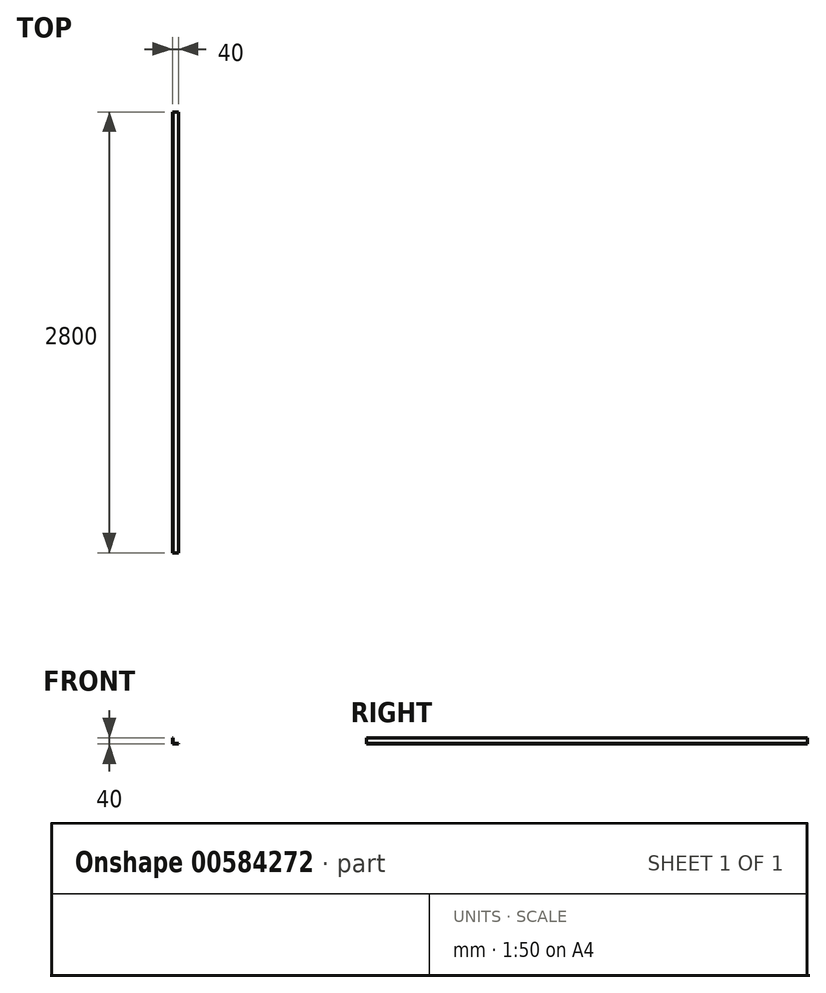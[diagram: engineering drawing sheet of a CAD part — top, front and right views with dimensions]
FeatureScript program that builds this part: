
annotation { "Feature Type Name" : "Feature", "Feature Type Description" : "" }
export const myFeature = defineFeature(function(context is Context, id is Id, definition is map)
    precondition{}
    {
        {
            var Q0;
            Q0=qCreatedBy(makeId("Front.planeOp"),FACE);
            var sketch = newSketch(context, id + "F0", { "sketchPlane" : qUnion([Q0])});
            skLineSegment(sketch, "E0", {"start": v(0, 0) * mm, "end": v(0, 40) * mm});
            skLineSegment(sketch, "E1", {"start": v(0, 40) * mm, "end": v(4, 40) * mm});
            skLineSegment(sketch, "E2", {"start": v(4, 40) * mm, "end": v(4, 4) * mm});
            skLineSegment(sketch, "E3", {"start": v(4, 4) * mm, "end": v(40, 4) * mm});
            skLineSegment(sketch, "E4", {"start": v(40, 4) * mm, "end": v(40, 0) * mm});
            skLineSegment(sketch, "E5", {"start": v(40, 0) * mm, "end": v(0, 0) * mm});
            skSolve(sketch);
        }
        {
            var Q0;
            Q0 = qSketchRegion(id + "F0", true);
            extrude(context, id + "F1", {"entities" : qUnion([Q0]), "depth" : 2800 * mm, "offsetDistance" : 25 * mm});
        }
    });
